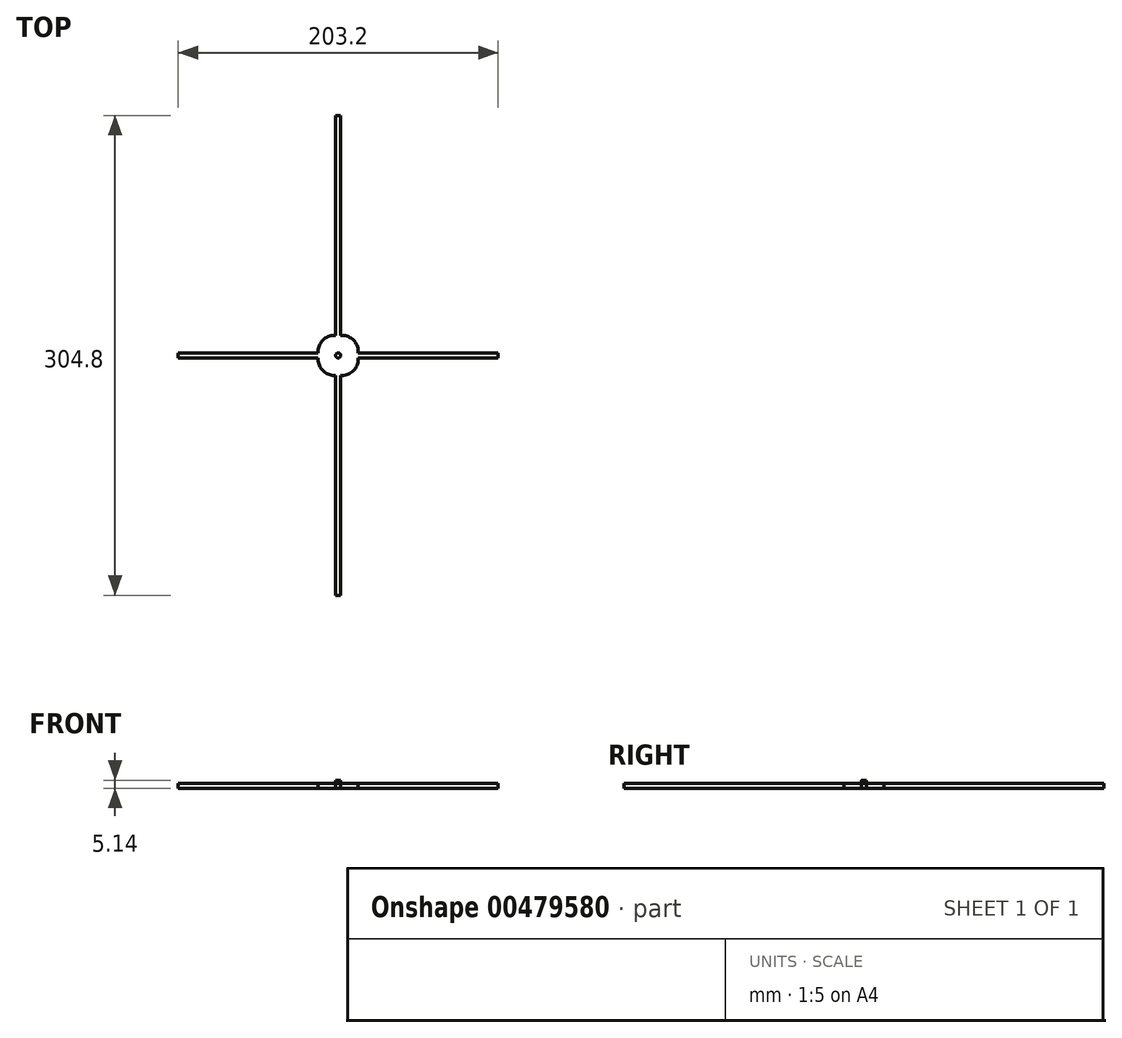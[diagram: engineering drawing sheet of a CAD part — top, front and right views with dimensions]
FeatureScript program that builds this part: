
annotation { "Feature Type Name" : "Feature", "Feature Type Description" : "" }
export const myFeature = defineFeature(function(context is Context, id is Id, definition is map)
    precondition{}
    {
        {
            var Q0;
            Q0=qCreatedBy(makeId("Top.planeOp"),FACE);
            var sketch = newSketch(context, id + "F0", { "sketchPlane" : qUnion([Q0])});
            skLineSegment(sketch, "E0.bottom", {"start": v(101.6, -1.59) * mm, "end": v(-101.6, -1.59) * mm});
            skLineSegment(sketch, "E0.top", {"start": v(101.6, 1.59) * mm, "end": v(-101.6, 1.59) * mm});
            skLineSegment(sketch, "E0.left", {"start": v(101.6, -1.59) * mm, "end": v(101.6, 1.59) * mm});
            skLineSegment(sketch, "E0.right", {"start": v(-101.6, -1.59) * mm, "end": v(-101.6, 1.59) * mm});
            skPoint(sketch, "E0.middle", {"position": v(0, 0) * mm});
            skLineSegment(sketch, "E1.bottom", {"start": v(1.59, -152.4) * mm, "end": v(-1.59, -152.4) * mm});
            skLineSegment(sketch, "E1.top", {"start": v(1.59, 152.4) * mm, "end": v(-1.59, 152.4) * mm});
            skLineSegment(sketch, "E1.left", {"start": v(1.59, -152.4) * mm, "end": v(1.59, 152.4) * mm});
            skLineSegment(sketch, "E1.right", {"start": v(-1.59, -152.4) * mm, "end": v(-1.59, 152.4) * mm});
            skLineSegment(sketch, "E2.bottom", {"start": v(12.7, -12.7) * mm, "end": v(-12.7, -12.7) * mm});
            skLineSegment(sketch, "E2.top", {"start": v(12.7, 12.7) * mm, "end": v(-12.7, 12.7) * mm});
            skLineSegment(sketch, "E2.left", {"start": v(12.7, -12.7) * mm, "end": v(12.7, 12.7) * mm});
            skLineSegment(sketch, "E2.right", {"start": v(-12.7, -12.7) * mm, "end": v(-12.7, 12.7) * mm});
            skCircle(sketch, "E3", {"center": v(0, 0) * mm, "radius": 1.59 * mm});
            skSolve(sketch);
        }
        {
            var Q0;
            {var subQ0=sQuery(id+"F0.wireOp",EDGE,"E2.right");var subQ1=sQuery(id+"F0.wireOp",EDGE,"E0.top");var subQ2=makeQuery(id+"F0.imprint","INTERSECT",VERTEX,{"derivedFrom":[subQ1,subQ0]});Q0=makeQuery(id+"F0.imprint","IMPRINT",FACE,{"disambiguationData":[TD([[makeQuery(id+"F0.imprint","IMPRINT",EDGE,{"disambiguationData":[TD([[subQ2,1.0]])],"derivedFrom":subQ1}),-1.0]])]});}
            var Q1;
            {var subQ0=sQuery(id+"F0.wireOp",EDGE,"E2.left");var subQ1=sQuery(id+"F0.wireOp",EDGE,"E0.top");var subQ2=makeQuery(id+"F0.imprint","INTERSECT",VERTEX,{"derivedFrom":[subQ1,subQ0]});Q1=makeQuery(id+"F0.imprint","IMPRINT",FACE,{"disambiguationData":[TD([[makeQuery(id+"F0.imprint","IMPRINT",EDGE,{"disambiguationData":[TD([[subQ2,-1.0]])],"derivedFrom":subQ1}),-1.0]])]});}
            var Q2;
            {var subQ0=sQuery(id+"F0.wireOp",EDGE,"E2.left");var subQ1=sQuery(id+"F0.wireOp",EDGE,"E0.bottom");var subQ2=makeQuery(id+"F0.imprint","INTERSECT",VERTEX,{"derivedFrom":[subQ1,subQ0]});Q2=makeQuery(id+"F0.imprint","IMPRINT",FACE,{"disambiguationData":[TD([[makeQuery(id+"F0.imprint","IMPRINT",EDGE,{"disambiguationData":[TD([[subQ2,-1.0]])],"derivedFrom":subQ1}),1.0]])]});}
            var Q3;
            {var subQ0=sQuery(id+"F0.wireOp",EDGE,"E2.right");var subQ1=sQuery(id+"F0.wireOp",EDGE,"E0.bottom");var subQ2=makeQuery(id+"F0.imprint","INTERSECT",VERTEX,{"derivedFrom":[subQ1,subQ0]});Q3=makeQuery(id+"F0.imprint","IMPRINT",FACE,{"disambiguationData":[TD([[makeQuery(id+"F0.imprint","IMPRINT",EDGE,{"disambiguationData":[TD([[subQ2,1.0]])],"derivedFrom":subQ1}),1.0]])]});}
            var Q4;
            {var subQ0=sQuery(id+"F0.wireOp",EDGE,"E1.top");Q4=makeQuery(id+"F0.imprint","IMPRINT",FACE,{"disambiguationData":[TD([[makeQuery(id+"F0.imprint","IMPRINT",EDGE,{"derivedFrom":subQ0}),1.0]])]});}
            var Q5;
            {var subQ3=sQuery(id+"F0.wireOp",EDGE,"E0.top");var subQ5=sQuery(id+"F0.wireOp",EDGE,"E1.left");var subQ7=makeQuery(id+"F0.imprint","INTERSECT",VERTEX,{"derivedFrom":[subQ3,subQ5]});Q5=makeQuery(id+"F0.imprint","IMPRINT",FACE,{"disambiguationData":[TD([[makeQuery(id+"F0.imprint","IMPRINT",EDGE,{"disambiguationData":[TD([[subQ7,-1.0]])],"derivedFrom":subQ3}),-1.0]])]});}
            var Q6;
            {var subQ4=sQuery(id+"F0.wireOp",EDGE,"E0.bottom");var subQ6=sQuery(id+"F0.wireOp",EDGE,"E2.left");var subQ8=makeQuery(id+"F0.imprint","INTERSECT",VERTEX,{"derivedFrom":[subQ4,subQ6]});Q6=makeQuery(id+"F0.imprint","IMPRINT",FACE,{"disambiguationData":[TD([[makeQuery(id+"F0.imprint","IMPRINT",EDGE,{"disambiguationData":[TD([[subQ8,-1.0]])],"derivedFrom":subQ4}),-1.0]])]});}
            var Q7;
            {var subQ4=sQuery(id+"F0.wireOp",EDGE,"E2.right");var subQ6=sQuery(id+"F0.wireOp",EDGE,"E0.bottom");var subQ8=makeQuery(id+"F0.imprint","INTERSECT",VERTEX,{"derivedFrom":[subQ6,subQ4]});Q7=makeQuery(id+"F0.imprint","IMPRINT",FACE,{"disambiguationData":[TD([[makeQuery(id+"F0.imprint","IMPRINT",EDGE,{"disambiguationData":[TD([[subQ8,1.0]])],"derivedFrom":subQ6}),-1.0]])]});}
            var Q8;
            {var subQ3=sQuery(id+"F0.wireOp",EDGE,"E0.bottom");var subQ6=sQuery(id+"F0.wireOp",EDGE,"E1.left");var subQ8=makeQuery(id+"F0.imprint","INTERSECT",VERTEX,{"derivedFrom":[subQ3,subQ6]});Q8=makeQuery(id+"F0.imprint","IMPRINT",FACE,{"disambiguationData":[TD([[makeQuery(id+"F0.imprint","IMPRINT",EDGE,{"disambiguationData":[TD([[subQ8,-1.0]])],"derivedFrom":subQ3}),1.0]])]});}
            var Q9;
            {var subQ0=sQuery(id+"F0.wireOp",EDGE,"E1.bottom");Q9=makeQuery(id+"F0.imprint","IMPRINT",FACE,{"disambiguationData":[TD([[makeQuery(id+"F0.imprint","IMPRINT",EDGE,{"derivedFrom":subQ0}),-1.0]])]});}
            var Q10;
            {var subQ0=sQuery(id+"F0.wireOp",EDGE,"E0.right");Q10=makeQuery(id+"F0.imprint","IMPRINT",FACE,{"disambiguationData":[TD([[makeQuery(id+"F0.imprint","IMPRINT",EDGE,{"derivedFrom":subQ0}),-1.0]])]});}
            var Q11;
            {var subQ0=sQuery(id+"F0.wireOp",EDGE,"E0.left");Q11=makeQuery(id+"F0.imprint","IMPRINT",FACE,{"disambiguationData":[TD([[makeQuery(id+"F0.imprint","IMPRINT",EDGE,{"derivedFrom":subQ0}),1.0]])]});}
            var Q12;
            {var subQ0=sQuery(id+"F0.wireOp",EDGE,"E3");var subQ1=sQuery(id+"F0.wireOp",EDGE,"E0.top");var subQ2=makeQuery(id+"F0.imprint","INTERSECT",VERTEX,{"derivedFrom":[subQ1,subQ0]});Q12=makeQuery(id+"F0.imprint","IMPRINT",FACE,{"disambiguationData":[TD([[makeQuery(id+"F0.imprint","IMPRINT",EDGE,{"disambiguationData":[TD([[subQ2,-1.0]])],"derivedFrom":subQ1}),1.0]])]});}
            var Q13;
            {var subQ0=sQuery(id+"F0.wireOp",EDGE,"E3");var subQ1=makeQuery(id+"F0.imprint","INTERSECT",VERTEX,{"derivedFrom":[sQuery(id+"F0.wireOp",EDGE,"E0.top"),subQ0]});Q13=makeQuery(id+"F0.imprint","IMPRINT",FACE,{"disambiguationData":[TD([[makeQuery(id+"F0.imprint","IMPRINT",EDGE,{"disambiguationData":[TD([[subQ1,1.0]])],"derivedFrom":subQ0}),1.0]])]});}
            var Q14;
            {var subQ0=sQuery(id+"F0.wireOp",EDGE,"E1.left");var subQ1=sQuery(id+"F0.wireOp",EDGE,"E0.top");var subQ2=makeQuery(id+"F0.imprint","INTERSECT",VERTEX,{"derivedFrom":[subQ1,subQ0]});Q14=makeQuery(id+"F0.imprint","IMPRINT",FACE,{"disambiguationData":[TD([[makeQuery(id+"F0.imprint","IMPRINT",EDGE,{"disambiguationData":[TD([[subQ2,-1.0]])],"derivedFrom":subQ1}),1.0]])]});}
            var Q15;
            {var subQ0=sQuery(id+"F0.wireOp",EDGE,"E3");var subQ1=sQuery(id+"F0.wireOp",EDGE,"E0.bottom");var subQ2=makeQuery(id+"F0.imprint","INTERSECT",VERTEX,{"derivedFrom":[subQ1,subQ0]});Q15=makeQuery(id+"F0.imprint","IMPRINT",FACE,{"disambiguationData":[TD([[makeQuery(id+"F0.imprint","IMPRINT",EDGE,{"disambiguationData":[TD([[subQ2,-1.0]])],"derivedFrom":subQ1}),-1.0]])]});}
            var Q16;
            {var subQ0=sQuery(id+"F0.wireOp",EDGE,"E1.left");var subQ1=sQuery(id+"F0.wireOp",EDGE,"E0.bottom");var subQ2=makeQuery(id+"F0.imprint","INTERSECT",VERTEX,{"derivedFrom":[subQ1,subQ0]});Q16=makeQuery(id+"F0.imprint","IMPRINT",FACE,{"disambiguationData":[TD([[makeQuery(id+"F0.imprint","IMPRINT",EDGE,{"disambiguationData":[TD([[subQ2,-1.0]])],"derivedFrom":subQ1}),-1.0]])]});}
            extrude(context, id + "F1", {"entities" : qUnion([Q0, Q1, Q2, Q3, Q4, Q5, Q6, Q7, Q8, Q9, Q10, Q11, Q12, Q13, Q14, Q15, Q16]), "depth" : 3.17 * mm});
        }
        {
            var Q0;
            {var subQ0=sQuery(id+"F0.wireOp",EDGE,"E3");var subQ1=makeQuery(id+"F0.imprint","INTERSECT",VERTEX,{"derivedFrom":[sQuery(id+"F0.wireOp",EDGE,"E0.top"),subQ0]});Q0=makeQuery(id+"F0.imprint","IMPRINT",FACE,{"disambiguationData":[TD([[makeQuery(id+"F0.imprint","IMPRINT",EDGE,{"disambiguationData":[TD([[subQ1,1.0]])],"derivedFrom":subQ0}),1.0]])]});}
            extrude(context, id + "F2", {"entities" : qUnion([Q0]), "operationType" : NewBodyOperationType.ADD, "depth" : 5.14 * mm});
        }
        {
            var Q0;
            Q0=makeQuery(id+"F1.opExtrude","SWEPT_EDGE",EDGE,{"disambiguationData":[OSD([sQuery(id+"F0.wireOp",EDGE,"E2.bottom"),sQuery(id+"F0.wireOp",EDGE,"E2.left")])]});
            var Q1;
            Q1=makeQuery(id+"F1.opExtrude","SWEPT_EDGE",EDGE,{"disambiguationData":[OSD([sQuery(id+"F0.wireOp",EDGE,"E2.bottom"),sQuery(id+"F0.wireOp",EDGE,"E2.right")])]});
            var Q2;
            Q2=makeQuery(id+"F1.opExtrude","SWEPT_EDGE",EDGE,{"disambiguationData":[OSD([sQuery(id+"F0.wireOp",EDGE,"E2.top"),sQuery(id+"F0.wireOp",EDGE,"E2.left")])]});
            var Q3;
            Q3=makeQuery(id+"F1.opExtrude","SWEPT_EDGE",EDGE,{"disambiguationData":[OSD([sQuery(id+"F0.wireOp",EDGE,"E2.top"),sQuery(id+"F0.wireOp",EDGE,"E2.right")])]});
            fillet(context, id + "F3", {"entities" : qUnion([Q0, Q1, Q2, Q3]), "radius" : 10.16 * mm, "tangentPropagation" : true, "allowEdgeOverflow" : false});
        }
    });
